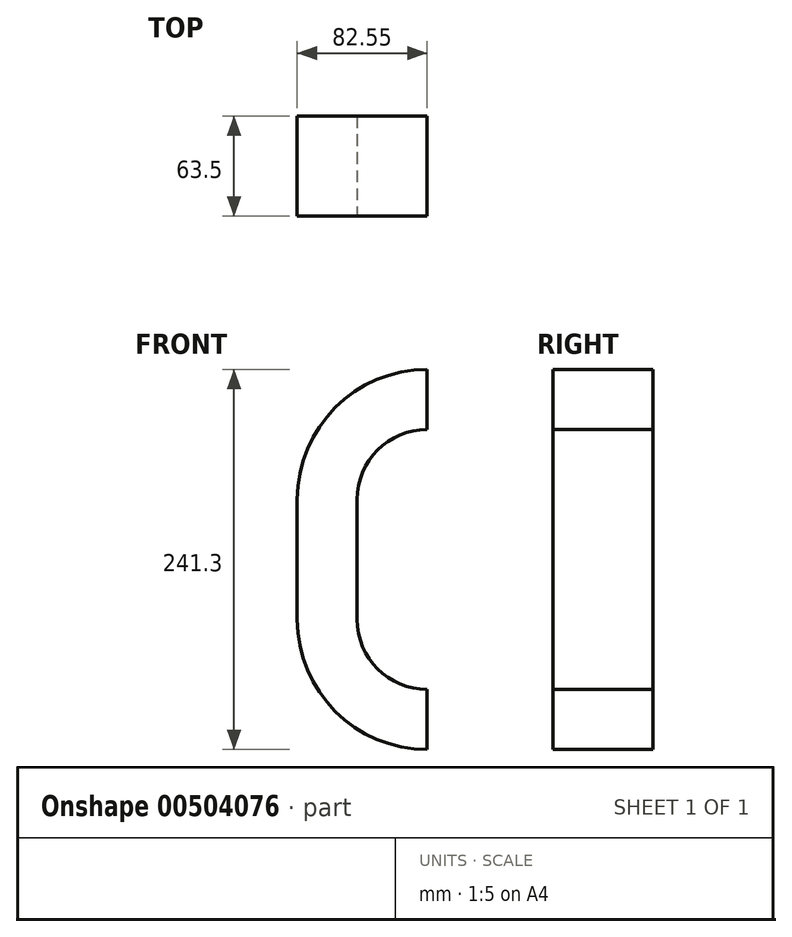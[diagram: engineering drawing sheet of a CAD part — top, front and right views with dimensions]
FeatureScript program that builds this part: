
annotation { "Feature Type Name" : "Feature", "Feature Type Description" : "" }
export const myFeature = defineFeature(function(context is Context, id is Id, definition is map)
    precondition{}
    {
        {
            var Q0;
            Q0=qCreatedBy(makeId("Front.planeOp"),FACE);
            var sketch = newSketch(context, id + "F0", { "sketchPlane" : qUnion([Q0])});
            skArc(sketch, "E0", {"start": v(0, 101.6) * mm, "mid": v(-44.9, 83) * mm, "end": v(-63.5, 38.1) * mm});
            skLineSegment(sketch, "E1", {"start": v(-63.5, 38.1) * mm, "end": v(-63.5, 0) * mm});
            skArc(sketch, "E2", {"start": v(-63.5, -38.1) * mm, "mid": v(-44.9, -83) * mm, "end": v(0, -101.6) * mm});
            skLineSegment(sketch, "E3", {"start": v(0, 0) * mm, "end": v(145.5, 0) * mm, "construction": true});
            skLineSegment(sketch, "E4", {"start": v(-63.5, 0) * mm, "end": v(-63.5, -38.1) * mm});
            skSolve(sketch);
        }
        {
            var Q0;
            Q0=qCreatedBy(makeId("Top.planeOp"),FACE);
            var sketch = newSketch(context, id + "F1", { "sketchPlane" : qUnion([Q0])});
            skLineSegment(sketch, "E5", {"start": v(-44.45, 31.75) * mm, "end": v(-44.45, -31.75) * mm});
            skLineSegment(sketch, "E6", {"start": v(-44.45, -31.75) * mm, "end": v(-82.55, -31.75) * mm});
            skLineSegment(sketch, "E7", {"start": v(-82.55, -31.75) * mm, "end": v(-82.55, 31.75) * mm});
            skLineSegment(sketch, "E8", {"start": v(-82.55, 31.75) * mm, "end": v(-44.45, 31.75) * mm});
            skLineSegment(sketch, "E9", {"start": v(-63.5, -31.75) * mm, "end": v(-63.5, 31.75) * mm, "construction": true});
            skPoint(sketch, "E9.endSnap0", {"position": v(-63.5, -31.75) * mm});
            skSolve(sketch);
        }
        {
            var Q0;
            Q0=makeQuery(id+"F1.imprint","IMPRINT",FACE,{"disambiguationData":[TD([[makeQuery(id+"F1.imprint","IMPRINT",EDGE,{"derivedFrom":sQuery(id+"F1.wireOp",EDGE,"E5")}),-1.0]])]});
            var Q1;
            Q1=sQuery(id+"F0.wireOp",EDGE,"E1");
            var Q2;
            Q2=sQuery(id+"F0.wireOp",EDGE,"E0");
            sweep(context, id + "F2", {"profiles" : qUnion([Q0]), "path" : qUnion([Q1, Q2])});
        }
        {
            var Q0;
            Q0=makeQuery(id+"F1.imprint","IMPRINT",FACE,{"disambiguationData":[TD([[makeQuery(id+"F1.imprint","IMPRINT",EDGE,{"derivedFrom":sQuery(id+"F1.wireOp",EDGE,"E5")}),-1.0]])]});
            var Q1;
            Q1=sQuery(id+"F0.wireOp",EDGE,"E4");
            var Q2;
            Q2=sQuery(id+"F0.wireOp",EDGE,"E2");
            sweep(context, id + "F3", {"operationType" : NewBodyOperationType.ADD, "profiles" : qUnion([Q0]), "path" : qUnion([Q1, Q2])});
        }
    });
